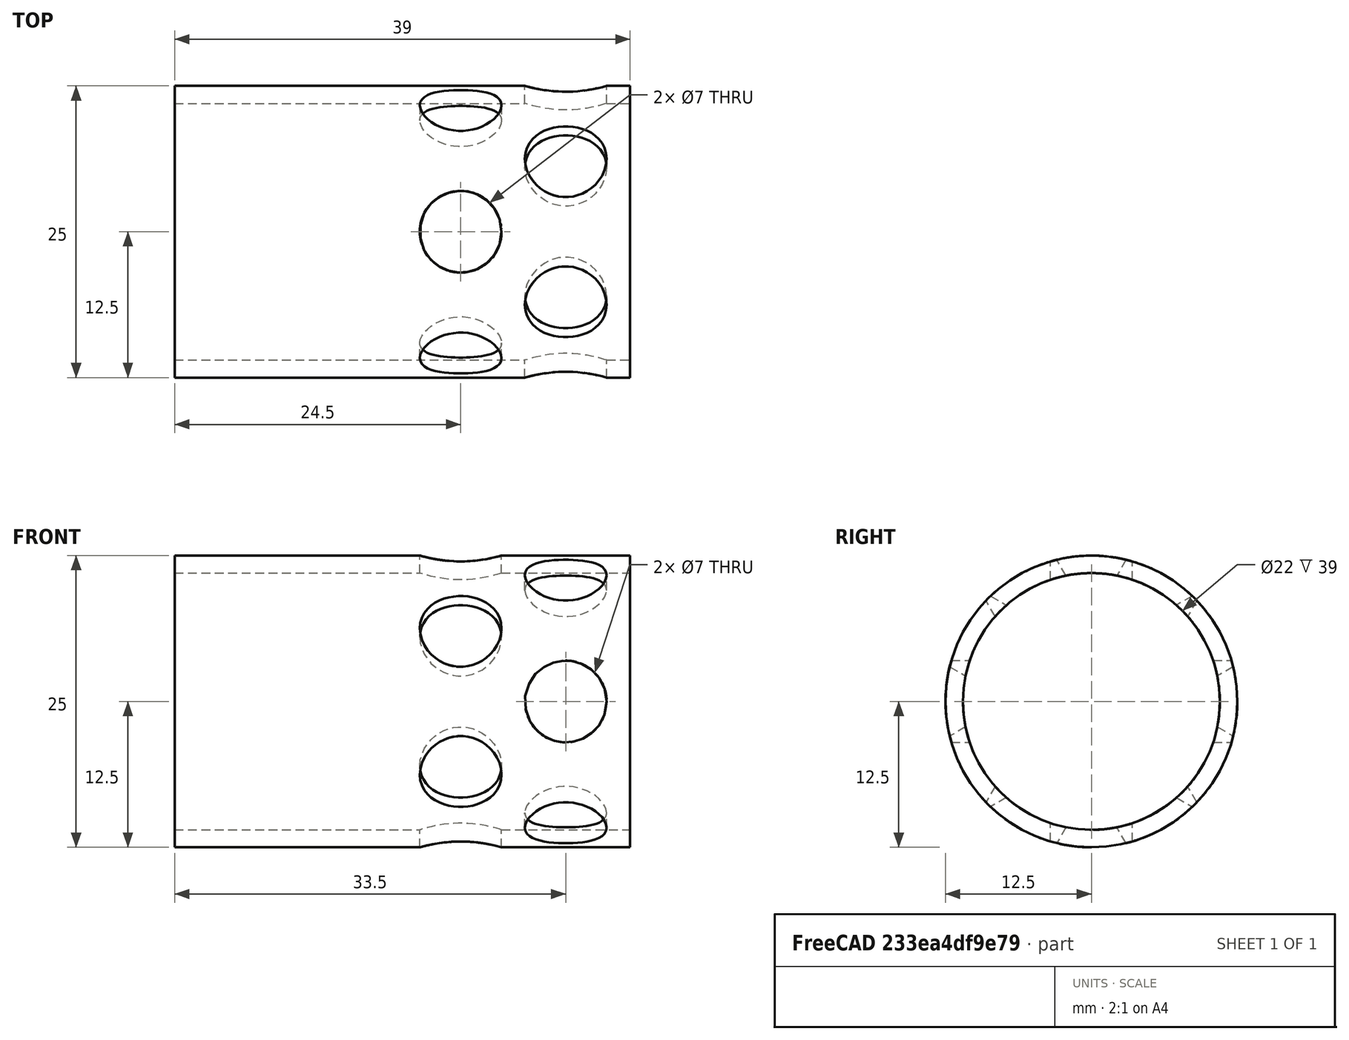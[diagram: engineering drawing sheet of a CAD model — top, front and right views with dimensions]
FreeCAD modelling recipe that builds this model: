
FCSTD DOCUMENT  (FreeCAD 0.17R13541 (Git))
Label: ERG-T-03-SC-01
License: All rights reserved
LicenseURL: http://en.wikipedia.org/wiki/All_rights_reserved
objects: Drawing::FeatureViewPython×9, Part::Cylinder×8, Part::MultiFuse×3, Part::Cut×2, Drawing::FeatureViewPart×2, Drawing::FeaturePage×1
note: 13 computed .brp shape members not serialized (recipe doc carries the construction recipe); baked Part::Feature solids carry a one-line shape summary decoded from their .brp

FEATURE [Part::Cylinder] Cylinder070  label="Cylinder075"
  Angle = 360
  AttacherType = Attacher::AttachEngine3D
  Height = 50
  Placement = pos=(214.2,-21.6506,12.5) rot=(-1,0,0;2.0944rad)
  Radius = 3.5
FEATURE [Part::Cylinder] Cylinder073  label="Cylinder082"
  Angle = 360
  AttacherType = Attacher::AttachEngine3D
  Height = 50
  Placement = pos=(214.2,-21.6506,12.5) rot=(-1,0,0;2.0944rad)
  Radius = 3.5
FEATURE [Part::Cylinder] Cylinder078  label="Cylinder087"
  Angle = 360
  AttacherType = Attacher::AttachEngine3D
  Height = 50
  Placement = pos=(214.2,21.6506,12.5) rot=(1,0,0;2.0944rad)
  Radius = 3.5
FEATURE [Part::Cylinder] Cylinder079  label="Cylinder088"
  Angle = 360
  AttacherType = Attacher::AttachEngine3D
  Height = 50
  Placement = pos=(214.2,21.6506,12.5) rot=(1,0,0;2.0944rad)
  Radius = 3.5
FEATURE [Part::Cylinder] Cylinder081  label="Cylinder090"
  Angle = 360
  AttacherType = Attacher::AttachEngine3D
  Height = 50
  Placement = pos=(214.2,0,-25) rot=(0,1,0;0rad)
  Radius = 3.5
FEATURE [Part::MultiFuse] Fusion016
  Placement = pos=(37.5,0,0) rot=(1,0,0;0rad)
  Shapes = -> [Cylinder081,Cylinder070,Cylinder078]
FEATURE [Part::Cylinder] Cylinder082  label="Cylinder078"
  Angle = 360
  AttacherType = Attacher::AttachEngine3D
  Height = 50
  Placement = pos=(214.2,0,-25) rot=(0,1,0;0rad)
  Radius = 3.5
FEATURE [Part::MultiFuse] Fusion018
  Placement = pos=(46.5,0,0) rot=(1,0,0;0.523599rad)
  Shapes = -> [Cylinder082,Cylinder073,Cylinder079]
FEATURE [Part::MultiFuse] Fusion  label="holesticks"
  Shapes = -> [Fusion016,Fusion018]
FEATURE [Part::Cylinder] Cylinder090  label="Cylinder098"
  Angle = 360
  AttacherType = Attacher::AttachEngine3D
  Height = 39
  Placement = pos=(227.2,0,0) rot=(0,1,0;1.5708rad)
  Radius = 12.5
FEATURE [Part::Cylinder] Cylinder071  label="Cylinder081"
  Angle = 360
  AttacherType = Attacher::AttachEngine3D
  Height = 39
  Placement = pos=(227.2,0,0) rot=(0,1,0;1.5708rad)
  Radius = 11
FEATURE [Part::Cut] Cut  label="body"
  Base = -> Cylinder090
  Tool = -> Cylinder071
FEATURE [Part::Cut] Cut001  label="CAP"
  Base = -> Cut
  Tool = -> Fusion
FEATURE [Drawing::FeatureViewPart] Ortho  label="Ortho_0_0"
  Direction = (1,0,0)
  HiddenWidth = 0.15
  LineWidth = 0.35
  Rotation = -90
  Scale = 3
  ShowHiddenLines = false
  ShowSmoothLines = false
  Source = -> Cut001
  Tolerance = 0.05
  ViewResult = <blob: 12799 chars omitted>
  Visible = true
  X = 75.8333
  Y = 81.5
FEATURE [Drawing::FeatureViewPart] Ortho001  label="Ortho_1_0"
  Direction = (0,1,0)
  HiddenWidth = 0.15
  LineWidth = 0.35
  Rotation = -90
  Scale = 3
  ShowHiddenLines = true
  ShowSmoothLines = false
  Source = -> Cut001
  Tolerance = 0.05
  ViewResult = <blob: 56747 chars omitted>
  Visible = true
  X = 940.267
  Y = 81.5
FEATURE [Drawing::FeatureViewPython] dim001  # drawing view (typed FeaturePython)
  Rotation = 0
  ViewResult = <g> \n  <line x1="258.667000" y1="44.000000" x2="279.909689" y2="44.000000" style="stroke:rgb(255,0,0);stroke-width:0.10" />\n<line x1="258.667000" y1="119.000000" x2="279.909689" y2="119.000000" style="stroke:rgb(255,0,0);stroke-width:0.10" />\n<line x1="278.909689" y1="44.000000" x2="278.909689" y2="119.000000" style="stroke:rgb(255,0,0);stroke-width:0.10" /> \n  <polygon points="278.909689,119.000000 279.409689,117.000000 278.909689,116.500000 278.409689,117.000000" style="fill:rgb(255,0,0);stroke:rgb(255,0,0);stroke-width:0" /><polygon points="278.909689,44.000000 278.409689,46.000000 278.909689,46.500000 279.409689,46.000000" style="fill:rgb(255,0,0);stroke:rgb(255,0,0);stroke-width:0" /> \n  <text x="276.909689" y="81.500000" font-family="inherit" font-size="3.6" fill="rgb(0,0,0)" text-anchor="middle" transform="rotate(-90.000000 276.909689,81.500000)" >25</text> </g>
  Visible = true
  X = 0
  Y = 0
  arrowL1 = 2
  arrowL2 = 0.5
  arrowW = 1
  arrow_scheme = 0
  autoPlaceOffset = 2
  autoPlaceText = true
  click1_x = 278.91
  click1_y = 107.68
  click2_x = 278.91
  click2_y = 107.68
  comma_decimal_place = false
  dimension_line_overshoot = 1
  gap_datum_points = 0
  halfDimension_linear = false
  lineColor = rgb(255,0,0)
  strokeWidth = 0.1
  textFormat_linear = %(value)3.3f
  textRenderer_color = rgb(0,0,0)
  textRenderer_family = inherit
  textRenderer_size = 3.6
  unit_custom_scale = 1
  unit_scheme = 0
FEATURE [Drawing::FeatureViewPython] dim002  # drawing view (typed FeaturePython)
  Rotation = 0
  ViewResult = <g> \n  <line x1="258.667000" y1="48.500000" x2="270.490011" y2="48.500000" style="stroke:rgb(255,0,0);stroke-width:0.10" />\n<line x1="258.667000" y1="114.500000" x2="270.490011" y2="114.500000" style="stroke:rgb(255,0,0);stroke-width:0.10" />\n<line x1="269.490011" y1="48.500000" x2="269.490011" y2="114.500000" style="stroke:rgb(255,0,0);stroke-width:0.10" /> \n  <polygon points="269.490011,114.500000 269.990011,112.500000 269.490011,112.000000 268.990011,112.500000" style="fill:rgb(255,0,0);stroke:rgb(255,0,0);stroke-width:0" /><polygon points="269.490011,48.500000 268.990011,50.500000 269.490011,51.000000 269.990011,50.500000" style="fill:rgb(255,0,0);stroke:rgb(255,0,0);stroke-width:0" /> \n  <text x="267.490011" y="81.500000" font-family="inherit" font-size="3.6" fill="rgb(0,0,0)" text-anchor="middle" transform="rotate(-90.000000 267.490011,81.500000)" >22</text> </g>
  Visible = true
  X = 0
  Y = 0
  arrowL1 = 2
  arrowL2 = 0.5
  arrowW = 1
  arrow_scheme = 0
  autoPlaceOffset = 2
  autoPlaceText = true
  click1_x = 269.49
  click1_y = 115.772
  click2_x = 269.49
  click2_y = 115.772
  comma_decimal_place = false
  dimension_line_overshoot = 1
  gap_datum_points = 0
  halfDimension_linear = false
  lineColor = rgb(255,0,0)
  strokeWidth = 0.1
  textFormat_linear = %(value)3.3f
  textRenderer_color = rgb(0,0,0)
  textRenderer_family = inherit
  textRenderer_size = 3.6
  unit_custom_scale = 1
  unit_scheme = 0
FEATURE [Drawing::FeatureViewPython] dim003  # drawing view (typed FeaturePython)
  Rotation = 0
  ViewResult = <g> \n  <line x1="141.667000" y1="44.000000" x2="141.667000" y2="24.783144" style="stroke:rgb(255,0,0);stroke-width:0.10" />\n<line x1="258.667000" y1="44.000000" x2="258.667000" y2="24.783144" style="stroke:rgb(255,0,0);stroke-width:0.10" />\n<line x1="141.667000" y1="25.783144" x2="258.667000" y2="25.783144" style="stroke:rgb(255,0,0);stroke-width:0.10" /> \n  <polygon points="258.667000,25.783144 256.667000,25.283144 256.167000,25.783144 256.667000,26.283144" style="fill:rgb(255,0,0);stroke:rgb(255,0,0);stroke-width:0" /><polygon points="141.667000,25.783144 143.667000,26.283144 144.167000,25.783144 143.667000,25.283144" style="fill:rgb(255,0,0);stroke:rgb(255,0,0);stroke-width:0" /> \n  <text x="200.167000" y="23.783144" font-family="inherit" font-size="3.6" fill="rgb(0,0,0)" text-anchor="middle" transform="rotate(0.000000 200.167000,23.783144)" >39</text> </g>
  Visible = true
  X = 0
  Y = 0
  arrowL1 = 2
  arrowL2 = 0.5
  arrowW = 1
  arrow_scheme = 0
  autoPlaceOffset = 2
  autoPlaceText = true
  click1_x = 256.366
  click1_y = 25.7831
  click2_x = 256.366
  click2_y = 25.7831
  comma_decimal_place = false
  dimension_line_overshoot = 1
  gap_datum_points = 0
  halfDimension_linear = false
  lineColor = rgb(255,0,0)
  strokeWidth = 0.1
  textFormat_linear = %(value)3.3f
  textRenderer_color = rgb(0,0,0)
  textRenderer_family = inherit
  textRenderer_size = 3.6
  unit_custom_scale = 1
  unit_scheme = 0
FEATURE [Drawing::FeatureViewPython] dim004  # drawing view (typed FeaturePython)
  Rotation = 0
  ViewResult = <g> \n  <line x1="258.667000" y1="44.000000" x2="267.415370" y2="44.000000" style="stroke:rgb(255,0,0);stroke-width:0.10" />\n<line x1="258.667000" y1="48.500000" x2="267.415370" y2="48.500000" style="stroke:rgb(255,0,0);stroke-width:0.10" />\n<line x1="266.415370" y1="44.000000" x2="266.415370" y2="48.500000" style="stroke:rgb(255,0,0);stroke-width:0.10" /> \n  <polygon points="266.415370,48.500000 265.915370,50.500000 266.415370,51.000000 266.915370,50.500000" style="fill:rgb(255,0,0);stroke:rgb(255,0,0);stroke-width:0" /><polygon points="266.415370,44.000000 266.915370,42.000000 266.415370,41.500000 265.915370,42.000000" style="fill:rgb(255,0,0);stroke:rgb(255,0,0);stroke-width:0" /> \n  <text x="264.415370" y="46.250000" font-family="inherit" font-size="3.6" fill="rgb(0,0,0)" text-anchor="middle" transform="rotate(-90.000000 264.415370,46.250000)" >1.5</text> </g>
  Visible = true
  X = 0
  Y = 0
  arrowL1 = 2
  arrowL2 = 0.5
  arrowW = 1
  arrow_scheme = 0
  autoPlaceOffset = 2
  autoPlaceText = true
  click1_x = 266.415
  click1_y = 48.9202
  click2_x = 266.415
  click2_y = 48.9202
  comma_decimal_place = false
  dimension_line_overshoot = 1
  gap_datum_points = 0
  halfDimension_linear = false
  lineColor = rgb(255,0,0)
  strokeWidth = 0.1
  textFormat_linear = %(value)3.3f
  textRenderer_color = rgb(0,0,0)
  textRenderer_family = inherit
  textRenderer_size = 3.6
  unit_custom_scale = 1
  unit_scheme = 0
FEATURE [Drawing::FeatureViewPython] dim005  # drawing view (typed FeaturePython)
  Rotation = 0
  ViewResult = <g> \n  <line x1="158.167000" y1="55.573100" x2="158.167000" y2="40.879975" style="stroke:rgb(255,0,0);stroke-width:0.10" />\n<line x1="141.667000" y1="44.000000" x2="141.667000" y2="40.879975" style="stroke:rgb(255,0,0);stroke-width:0.10" />\n<line x1="158.167000" y1="41.879975" x2="141.667000" y2="41.879975" style="stroke:rgb(255,0,0);stroke-width:0.10" /> \n  <polygon points="141.667000,41.879975 143.667000,42.379975 144.167000,41.879975 143.667000,41.379975" style="fill:rgb(255,0,0);stroke:rgb(255,0,0);stroke-width:0" /><polygon points="158.167000,41.879975 156.167000,41.379975 155.667000,41.879975 156.167000,42.379975" style="fill:rgb(255,0,0);stroke:rgb(255,0,0);stroke-width:0" /> \n  <text x="149.917000" y="39.879975" font-family="inherit" font-size="3.6" fill="rgb(0,0,0)" text-anchor="middle" transform="rotate(0.000000 149.917000,39.879975)" >5.5</text> </g>
  Visible = true
  X = 0
  Y = 0
  arrowL1 = 2
  arrowL2 = 0.5
  arrowW = 1
  arrow_scheme = 0
  autoPlaceOffset = 2
  autoPlaceText = true
  click1_x = 147.089
  click1_y = 41.88
  click2_x = 147.089
  click2_y = 41.88
  comma_decimal_place = false
  dimension_line_overshoot = 1
  gap_datum_points = 0
  halfDimension_linear = false
  lineColor = rgb(255,0,0)
  strokeWidth = 0.1
  textFormat_linear = %(value)3.3f
  textRenderer_color = rgb(0,0,0)
  textRenderer_family = inherit
  textRenderer_size = 3.6
  unit_custom_scale = 1
  unit_scheme = 0
FEATURE [Drawing::FeatureViewPython] dim007  # drawing view (typed FeaturePython)
  Rotation = 0
  ViewResult = <g> \n  <line x1="185.167000" y1="72.593270" x2="185.167000" y2="33.823592" style="stroke:rgb(255,0,0);stroke-width:0.10" />\n<line x1="141.667000" y1="44.000000" x2="141.667000" y2="33.823592" style="stroke:rgb(255,0,0);stroke-width:0.10" />\n<line x1="185.167000" y1="34.823592" x2="141.667000" y2="34.823592" style="stroke:rgb(255,0,0);stroke-width:0.10" /> \n  <polygon points="141.667000,34.823592 143.667000,35.323592 144.167000,34.823592 143.667000,34.323592" style="fill:rgb(255,0,0);stroke:rgb(255,0,0);stroke-width:0" /><polygon points="185.167000,34.823592 183.167000,34.323592 182.667000,34.823592 183.167000,35.323592" style="fill:rgb(255,0,0);stroke:rgb(255,0,0);stroke-width:0" /> \n  <text x="163.417000" y="32.823592" font-family="inherit" font-size="3.6" fill="rgb(0,0,0)" text-anchor="middle" transform="rotate(0.000000 163.417000,32.823592)" >14.5</text> </g>
  Visible = true
  X = 0
  Y = 0
  arrowL1 = 2
  arrowL2 = 0.5
  arrowW = 1
  arrow_scheme = 0
  autoPlaceOffset = 2
  autoPlaceText = true
  click1_x = 155.021
  click1_y = 34.8236
  click2_x = 155.021
  click2_y = 34.8236
  comma_decimal_place = false
  dimension_line_overshoot = 1
  gap_datum_points = 0
  halfDimension_linear = false
  lineColor = rgb(255,0,0)
  strokeWidth = 0.1
  textFormat_linear = %(value)3.3f
  textRenderer_color = rgb(0,0,0)
  textRenderer_family = inherit
  textRenderer_size = 3.6
  unit_custom_scale = 1
  unit_scheme = 0
FEATURE [Drawing::FeatureViewPython] dia001  # drawing view (typed FeaturePython)
  Rotation = 0
  ViewResult = <g>  <circle cx ="75.833300" cy ="81.500000" r="0.250000" stroke="none" fill="rgb(255,0,0)" /> \n<line x1="32.659542" y1="53.489644" x2="103.517337" y2="99.460905" style="stroke:rgb(255,0,0);stroke-width:0.10" />\n<polygon points="48.149263,63.539095 49.554948,65.047090 50.246538,64.899770 50.099218,64.208180" style="fill:rgb(255,0,0);stroke:rgb(255,0,0);stroke-width:0" />\n<polygon points="103.517337,99.460905 102.111652,97.952910 101.420062,98.100230 101.567382,98.791820" style="fill:rgb(255,0,0);stroke:rgb(255,0,0);stroke-width:0" />\n<line x1="32.659542" y1="53.489644" x2="20.058616" y2="53.489644" style="stroke:rgb(255,0,0);stroke-width:0.10" />\n<text x="26.359079" y="51.489644" font-family="inherit" font-size="3.6" fill="rgb(0,0,0)" text-anchor="middle" transform="rotate(0.000000 26.359079,51.489644)" >Ø22</text> </g>
  Visible = true
  X = 0
  Y = 0
  arrowL1 = 2
  arrowL2 = 0.5
  arrowW = 1
  arrow_scheme = 0
  autoPlaceOffset = 2
  autoPlaceText = true
  centerPointDia = 0.5
  click1_x = 32.6595
  click1_y = 53.4896
  click2_x = 20.0586
  click2_y = 55.2898
  click3_x = 20.0586
  click3_y = 55.2898
  comma_decimal_place = false
  lineColor = rgb(255,0,0)
  strokeWidth = 0.1
  textFormat_circular = Ø%(value)3.3f
  textRenderer_color = rgb(0,0,0)
  textRenderer_family = inherit
  textRenderer_size = 3.6
  unit_custom_scale = 1
  unit_scheme = 0
FEATURE [Drawing::FeatureViewPython] dia002  # drawing view (typed FeaturePython)
  Rotation = 0
  ViewResult = <g>  <circle cx ="75.829311" cy ="81.476701" r="0.250000" stroke="none" fill="rgb(255,0,0)" /> \n<line x1="40.374394" y1="37.545615" x2="99.365901" y2="110.640159" style="stroke:rgb(255,0,0);stroke-width:0.10" />\n<polygon points="52.292721,52.313243 53.159706,54.183628 53.862816,54.258700 53.937888,53.555589" style="fill:rgb(255,0,0);stroke:rgb(255,0,0);stroke-width:0" />\n<polygon points="99.365901,110.640159 98.498916,108.769775 97.795805,108.694703 97.720733,109.397813" style="fill:rgb(255,0,0);stroke:rgb(255,0,0);stroke-width:0" />\n<line x1="40.374394" y1="37.545615" x2="29.830763" y2="37.545615" style="stroke:rgb(255,0,0);stroke-width:0.10" />\n<text x="35.102579" y="35.545615" font-family="inherit" font-size="3.6" fill="rgb(0,0,0)" text-anchor="middle" transform="rotate(0.000000 35.102579,35.545615)" >Ø 25</text> </g>
  Visible = true
  X = 0
  Y = 0
  arrowL1 = 2
  arrowL2 = 0.5
  arrowW = 1
  arrow_scheme = 0
  autoPlaceOffset = 2
  autoPlaceText = true
  centerPointDia = 0.5
  click1_x = 40.3744
  click1_y = 37.5456
  click2_x = 29.8308
  click2_y = 38.8314
  click3_x = 29.8308
  click3_y = 38.8314
  comma_decimal_place = false
  lineColor = rgb(255,0,0)
  strokeWidth = 0.1
  textFormat_circular = Ø%(value)3.0f
  textRenderer_color = rgb(0,0,0)
  textRenderer_family = inherit
  textRenderer_size = 3.6
  unit_custom_scale = 1
  unit_scheme = 0
FEATURE [Drawing::FeatureViewPython] dia003  # drawing view (typed FeaturePython)
  Rotation = 0
  ViewResult = <g>  <circle cx ="158.192843" cy ="81.468091" r="0.250000" stroke="none" fill="rgb(255,0,0)" /> \n<line x1="135.178680" y1="107.079741" x2="165.183398" y2="73.688549" style="stroke:rgb(255,0,0);stroke-width:0.10" />\n<polygon points="151.202288,89.247633 152.910960,88.094187 152.873242,87.388087 152.167142,87.425805" style="fill:rgb(255,0,0);stroke:rgb(255,0,0);stroke-width:0" />\n<polygon points="165.183398,73.688549 163.474725,74.841995 163.512443,75.548095 164.218543,75.510376" style="fill:rgb(255,0,0);stroke:rgb(255,0,0);stroke-width:0" />\n<line x1="135.178680" y1="107.079741" x2="119.483777" y2="107.079741" style="stroke:rgb(255,0,0);stroke-width:0.10" />\n<text x="127.331229" y="105.079741" font-family="inherit" font-size="3.6" fill="rgb(0,0,0)" text-anchor="middle" transform="rotate(0.000000 127.331229,105.079741)" >Ø7</text> </g>
  Visible = true
  X = 0
  Y = 0
  arrowL1 = 2
  arrowL2 = 0.5
  arrowW = 1
  arrow_scheme = 0
  autoPlaceOffset = 2
  autoPlaceText = true
  centerPointDia = 0.5
  click1_x = 135.179
  click1_y = 107.08
  click2_x = 119.484
  click2_y = 115.18
  click3_x = 119.484
  click3_y = 115.18
  comma_decimal_place = false
  lineColor = rgb(255,0,0)
  strokeWidth = 0.1
  textFormat_circular = Ø%(value)3.1f
  textRenderer_color = rgb(0,0,0)
  textRenderer_family = inherit
  textRenderer_size = 3.6
  unit_custom_scale = 1
  unit_scheme = 0
FEATURE [Drawing::FeaturePage] Page  label="PROJECTIONS"
  EditableTexts = Dr. Zoidberg | 11.04.2019 | x2.5 | Weight | ERG-T-03 | Sensor Cap | 2 | 1
  Group = -> [Ortho,Ortho001,dim001,dim002,dim003,dim004,dim005,dim007,dia001,dia002,dia003]
  Template = <path>//share/freecad/Mod/Drawing/Templates/A4_Landscape.svg
note: 1 file-system path scrubbed to <path> (originals preserved in the JSON sidecar)
